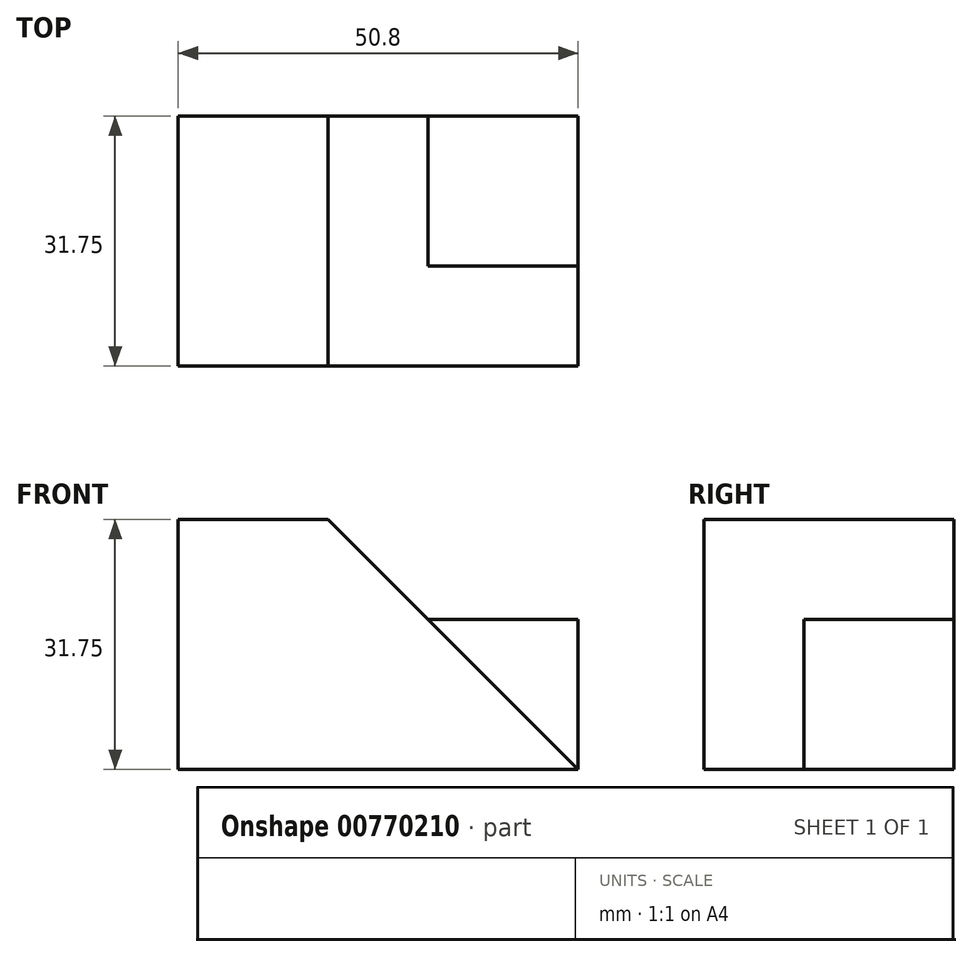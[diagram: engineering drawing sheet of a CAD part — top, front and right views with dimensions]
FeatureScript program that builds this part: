
annotation { "Feature Type Name" : "Feature", "Feature Type Description" : "" }
export const myFeature = defineFeature(function(context is Context, id is Id, definition is map)
    precondition{}
    {
        {
            var Q0;
            Q0=qCreatedBy(makeId("Front.planeOp"),FACE);
            var sketch = newSketch(context, id + "F0", { "sketchPlane" : qUnion([Q0])});
            skLineSegment(sketch, "E0", {"start": v(0, 0) * mm, "end": v(50.8, 0) * mm});
            skLineSegment(sketch, "E1", {"start": v(50.8, 0) * mm, "end": v(50.8, 31.75) * mm});
            skLineSegment(sketch, "E2", {"start": v(50.8, 31.75) * mm, "end": v(0, 31.75) * mm});
            skLineSegment(sketch, "E3", {"start": v(0, 31.75) * mm, "end": v(0, 0) * mm});
            skSolve(sketch);
        }
        {
            var Q0;
            Q0=makeQuery(id+"F0.imprint","IMPRINT",FACE,{"disambiguationData":[TD([[makeQuery(id+"F0.imprint","IMPRINT",EDGE,{"derivedFrom":sQuery(id+"F0.wireOp",EDGE,"E0")}),1.0]])]});
            extrude(context, id + "F1", {"entities" : qUnion([Q0]), "depth" : 31.75 * mm, "offsetDistance" : 25.4 * mm});
        }
        {
            var Q0;
            Q0=makeQuery(id+"F1.opExtrude","CAP_FACE",FACE,{"disambiguationData":[OSD([sQuery(id+"F0.wireOp",EDGE,"E0"),sQuery(id+"F0.wireOp",EDGE,"E1"),sQuery(id+"F0.wireOp",EDGE,"E2"),sQuery(id+"F0.wireOp",EDGE,"E3")])],"isStart":false});
            var sketch = newSketch(context, id + "F2", { "sketchPlane" : qUnion([Q0])});
            skLineSegment(sketch, "E4", {"start": v(0, 31.75) * mm, "end": v(19.05, 31.75) * mm});
            skLineSegment(sketch, "E5", {"start": v(19.05, 31.75) * mm, "end": v(50.8, 0) * mm});
            skLineSegment(sketch, "E6", {"start": v(19.05, 31.75) * mm, "end": v(31.75, 31.75) * mm});
            skLineSegment(sketch, "E7", {"start": v(31.75, 31.75) * mm, "end": v(31.75, 19.05) * mm});
            skSolve(sketch);
        }
        {
            var Q0;
            {var subQ0=sQuery(id+"F2.wireOp",EDGE,"E6");Q0=makeQuery(id+"F2.imprint","IMPRINT",FACE,{"disambiguationData":[TD([[makeQuery(id+"F2.imprint","IMPRINT",EDGE,{"derivedFrom":subQ0}),1.0]])]});}
            extrude(context, id + "F3", {"entities" : qUnion([Q0]), "operationType" : NewBodyOperationType.REMOVE, "oppositeDirection" : true, "depth" : 31.75 * mm, "offsetDistance" : 25.4 * mm});
        }
        {
            var Q0;
            Q0=makeQuery(id+"F1.opExtrude","CAP_FACE",FACE,{"disambiguationData":[OSD([sQuery(id+"F0.wireOp",EDGE,"E0"),sQuery(id+"F0.wireOp",EDGE,"E1"),sQuery(id+"F0.wireOp",EDGE,"E2"),sQuery(id+"F0.wireOp",EDGE,"E3")])],"isStart":false});
            var sketch = newSketch(context, id + "F4", { "sketchPlane" : qUnion([Q0])});
            skLineSegment(sketch, "E8", {"start": v(31.75, 19.05) * mm, "end": v(50.8, 0) * mm});
            skLineSegment(sketch, "E9", {"start": v(31.75, 19.05) * mm, "end": v(31.75, 31.75) * mm});
            skLineSegment(sketch, "E10", {"start": v(31.75, 31.75) * mm, "end": v(50.8, 31.75) * mm});
            skLineSegment(sketch, "E11", {"start": v(50.8, 31.75) * mm, "end": v(50.8, 0) * mm});
            skSolve(sketch);
        }
        {
            var Q0;
            Q0=makeQuery(id+"F4.imprint","IMPRINT",FACE,{"disambiguationData":[TD([[makeQuery(id+"F4.imprint","IMPRINT",EDGE,{"derivedFrom":sQuery(id+"F4.wireOp",EDGE,"E8")}),1.0]])]});
            extrude(context, id + "F5", {"entities" : qUnion([Q0]), "operationType" : NewBodyOperationType.REMOVE, "oppositeDirection" : true, "depth" : 12.7 * mm, "offsetDistance" : 25.4 * mm});
        }
        {
            var Q0;
            Q0=makeQuery(id+"F1.opExtrude","SWEPT_FACE",FACE,{"disambiguationData":[OSD([sQuery(id+"F0.wireOp",EDGE,"E1")])]});
            var sketch = newSketch(context, id + "F6", { "sketchPlane" : qUnion([Q0])});
            skLineSegment(sketch, "E12", {"start": v(-19.05, 31.75) * mm, "end": v(-19.05, 19.05) * mm});
            skLineSegment(sketch, "E13", {"start": v(-19.05, 19.05) * mm, "end": v(0, 19.05) * mm});
            skLineSegment(sketch, "E14", {"start": v(0, 19.05) * mm, "end": v(0, 31.75) * mm});
            skLineSegment(sketch, "E15", {"start": v(0, 31.75) * mm, "end": v(-19.05, 31.75) * mm});
            skSolve(sketch);
        }
        {
            var Q0;
            Q0=makeQuery(id+"F6.imprint","IMPRINT",FACE,{"disambiguationData":[TD([[makeQuery(id+"F6.imprint","IMPRINT",EDGE,{"derivedFrom":sQuery(id+"F6.wireOp",EDGE,"E12")}),-1.0]])]});
            extrude(context, id + "F7", {"entities" : qUnion([Q0]), "operationType" : NewBodyOperationType.REMOVE, "oppositeDirection" : true, "depth" : 19.05 * mm, "offsetDistance" : 25.4 * mm});
        }
    });
